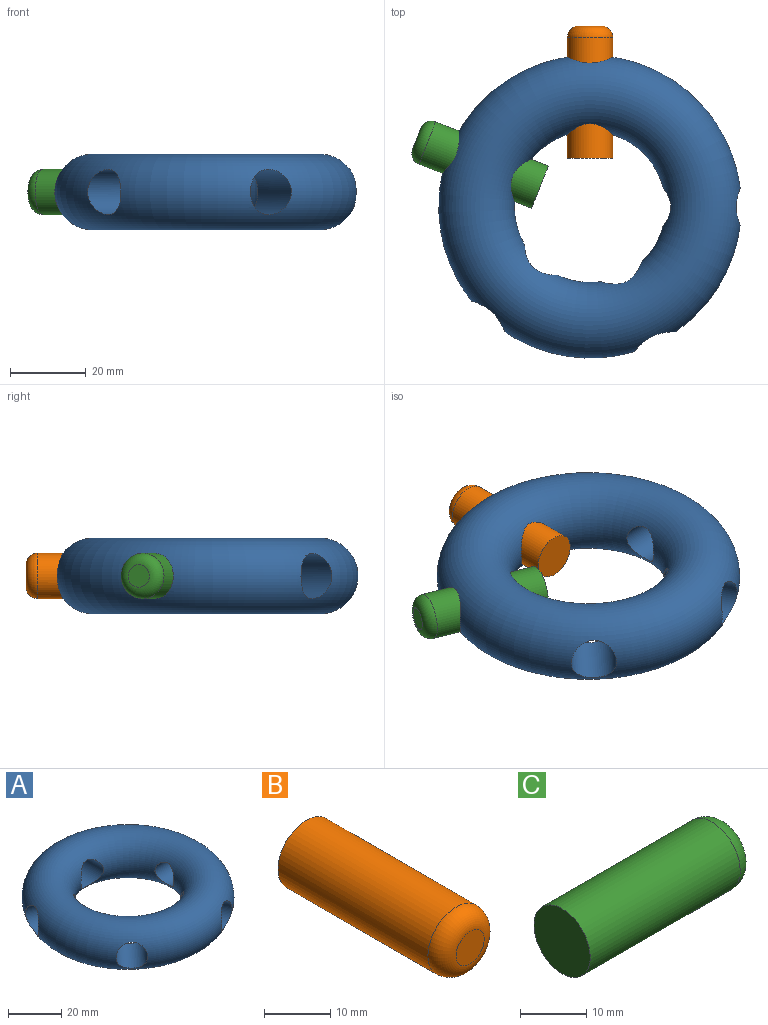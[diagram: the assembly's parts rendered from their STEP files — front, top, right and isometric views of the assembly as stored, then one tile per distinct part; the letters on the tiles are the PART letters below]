
ASSEMBLY  parts=3 mates=2
PART A: 6 faces, bbox 86.6x86.6x12 mm
  f0: torus R=30mm, axis (0,0,1), area 10719.3mm2, adj f1,f2,f3,f4,f5
  f1: cylinder r=6mm len=20.47mm, axis (0,-1,0), area 688.9mm2, adj f0
  f2: cylinder r=6mm len=23.65mm, axis (-0.43,0.9,0), area 688.9mm2, adj f0
  f3: cylinder r=6mm len=23.17mm, axis (0.68,0.73,0), area 689mm2, adj f0
  f4: cylinder r=6mm len=23.44mm, axis (0.93,-0.37,0), area 688.9mm2, adj f0
  f5: cylinder r=5mm len=20.32mm, axis (-1,0,0), area 591.8mm2, adj f0
PART B: 4 faces, bbox 13x35x13 mm
  f0: cylinder r=6mm len=32mm, axis (0,1,0), area 1206.4mm2, adj f2,f3
  f1: plane 6x6mm, normal (0,-1,0), area 28.3mm2, adj f3
  f2: plane 12x12mm, normal (0,1,0), area 113.1mm2, adj f0
  f3: torus R=3mm, axis (0,-1,0), area 145.4mm2, adj f0,f1
PART C: 4 faces, bbox 35x13x13 mm
  f0: cylinder r=6mm len=32mm, axis (-1,0,0), area 1206.4mm2, adj f2,f3
  f1: plane 6x6mm, normal (1,0,0), area 28.3mm2, adj f3
  f2: plane 12x12mm, normal (-1,0,0), area 113.1mm2, adj f0
  f3: torus R=3mm, axis (1,0,0), area 145.4mm2, adj f0,f1
PLACE A t=(1.79,-26.34,12.15)mm fixed
PLACE B rot(axis=(1,0,0),180deg) t=(72.94,-13.54,-66.79)mm
PLACE C rot(axis=(0,0,1),158.6deg) t=(11.38,36.98,-44.67)mm
MATE slider B.f0 <-> A.f1  axis (0,-1,0) through (1.79,2.46,12.15)mm
MATE slider A.f4 <-> C.f0  axis (0.93,-0.37,0) through (-35.15,-11.84,12.15)mm
